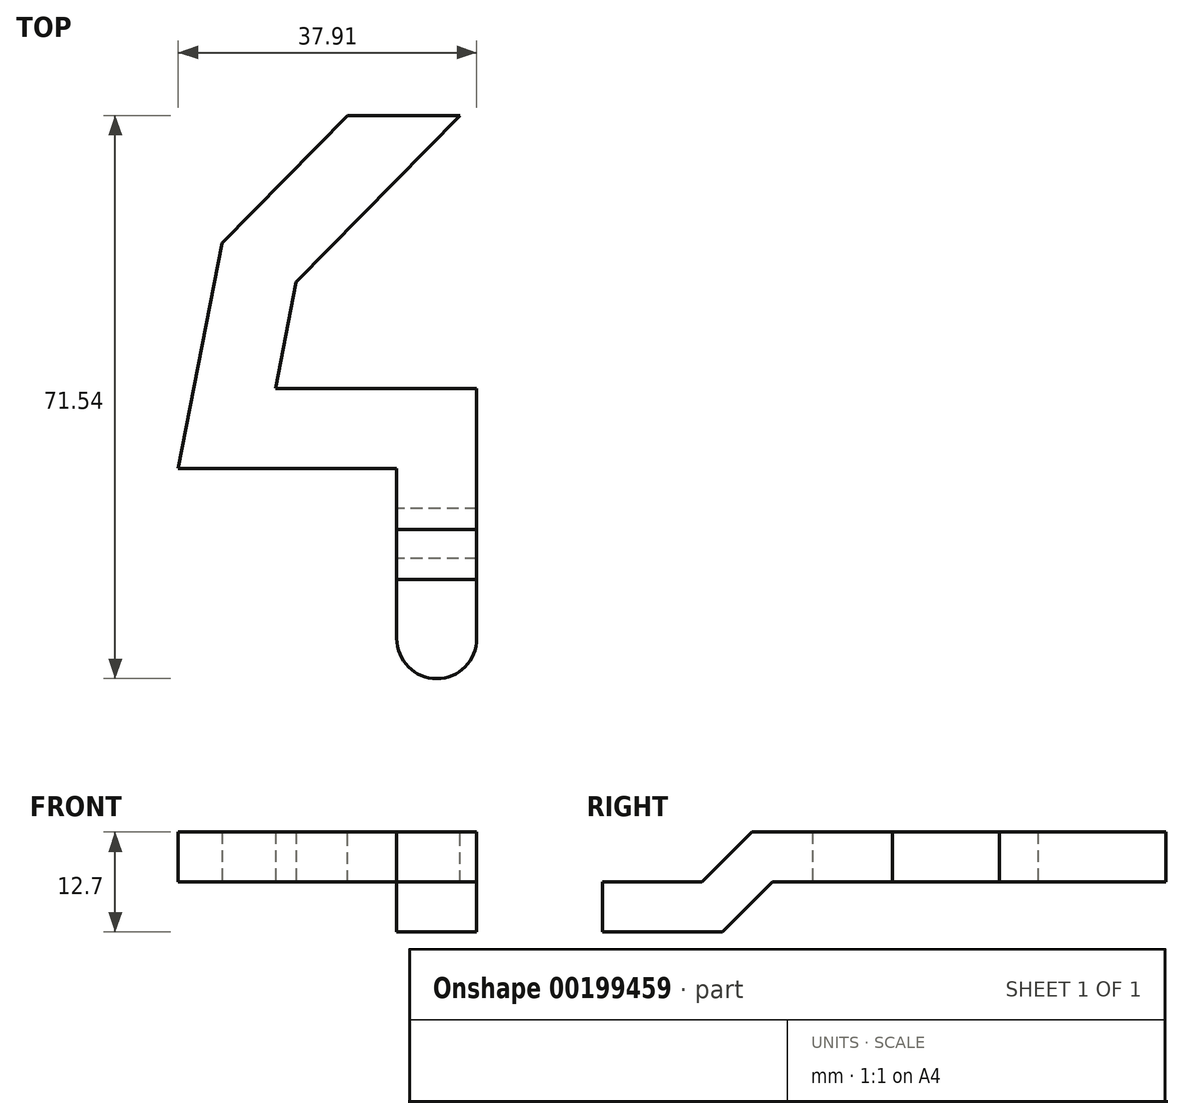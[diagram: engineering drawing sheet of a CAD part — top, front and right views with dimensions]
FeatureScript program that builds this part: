
annotation { "Feature Type Name" : "Feature", "Feature Type Description" : "" }
export const myFeature = defineFeature(function(context is Context, id is Id, definition is map)
    precondition{}
    {
        {
            var Q0;
            Q0=qCreatedBy(makeId("Top.planeOp"),FACE);
            var sketch = newSketch(context, id + "F0", { "sketchPlane" : qUnion([Q0])});
            skLineSegment(sketch, "E0", {"start": v(0, 0) * mm, "end": v(0, 26.67) * mm});
            skLineSegment(sketch, "E1", {"start": v(0, 26.67) * mm, "end": v(-26.67, 26.67) * mm});
            skLineSegment(sketch, "E2", {"start": v(-26.67, 26.67) * mm, "end": v(-22.57, 47.75) * mm});
            skLineSegment(sketch, "E3", {"start": v(-22.57, 47.75) * mm, "end": v(4.13, 74.93) * mm});
            skLineSegment(sketch, "E4.0", {"start": v(-17.88, 45.28) * mm, "end": v(7.76, 71.37) * mm});
            skLineSegment(sketch, "E4.1", {"start": v(-20.5, 31.75) * mm, "end": v(-17.88, 45.28) * mm});
            skLineSegment(sketch, "E4.2", {"start": v(5.08, 31.75) * mm, "end": v(-20.5, 31.75) * mm});
            skLineSegment(sketch, "E4.3", {"start": v(5.08, 0) * mm, "end": v(5.08, 31.75) * mm});
            skLineSegment(sketch, "E5.0", {"start": v(-27.27, 50.22) * mm, "end": v(0.5, 78.49) * mm});
            skLineSegment(sketch, "E5.1", {"start": v(-32.83, 21.6) * mm, "end": v(-27.27, 50.22) * mm});
            skLineSegment(sketch, "E5.2", {"start": v(-5.08, 21.6) * mm, "end": v(-32.83, 21.59) * mm});
            skLineSegment(sketch, "E5.3", {"start": v(-5.08, 0) * mm, "end": v(-5.08, 21.6) * mm});
            skCircle(sketch, "E6", {"center": v(4.13, 74.93) * mm, "radius": 5.08 * mm});
            skCircle(sketch, "E7", {"center": v(0, 0) * mm, "radius": 5.08 * mm});
            skSolve(sketch);
        }
        {
            var Q0;
            Q0=qCreatedBy(makeId("Right.planeOp"),FACE);
            var sketch = newSketch(context, id + "F1", { "sketchPlane" : qUnion([Q0])});
            skLineSegment(sketch, "E8", {"start": v(-5.08, 0) * mm, "end": v(10.16, 0) * mm});
            skLineSegment(sketch, "E9", {"start": v(10.16, 0) * mm, "end": v(16.5, 6.35) * mm});
            skLineSegment(sketch, "E10", {"start": v(16.5, 6.35) * mm, "end": v(66.46, 6.35) * mm});
            skLineSegment(sketch, "E11", {"start": v(66.46, 6.35) * mm, "end": v(66.46, 12.7) * mm});
            skLineSegment(sketch, "E12", {"start": v(66.46, 12.7) * mm, "end": v(13.88, 12.7) * mm});
            skLineSegment(sketch, "E13", {"start": v(13.88, 12.7) * mm, "end": v(7.53, 6.35) * mm});
            skLineSegment(sketch, "E14", {"start": v(7.53, 6.35) * mm, "end": v(-5.08, 6.35) * mm});
            skLineSegment(sketch, "E15", {"start": v(-5.08, 6.35) * mm, "end": v(-5.08, 0) * mm});
            skSolve(sketch);
        }
        {
            var Q0;
            Q0 = qSketchRegion(id + "F0", true);
            extrude(context, id + "F2", {"entities" : qUnion([Q0]), "depth" : 12.7 * mm});
        }
        {
            var Q0;
            Q0 = qSketchRegion(id + "F1", true);
            extrude(context, id + "F3", {"entities" : qUnion([Q0]), "operationType" : NewBodyOperationType.INTERSECT, "endBound" : BoundingType.SYMMETRIC, "depth" : 127 * mm});
        }
    });
